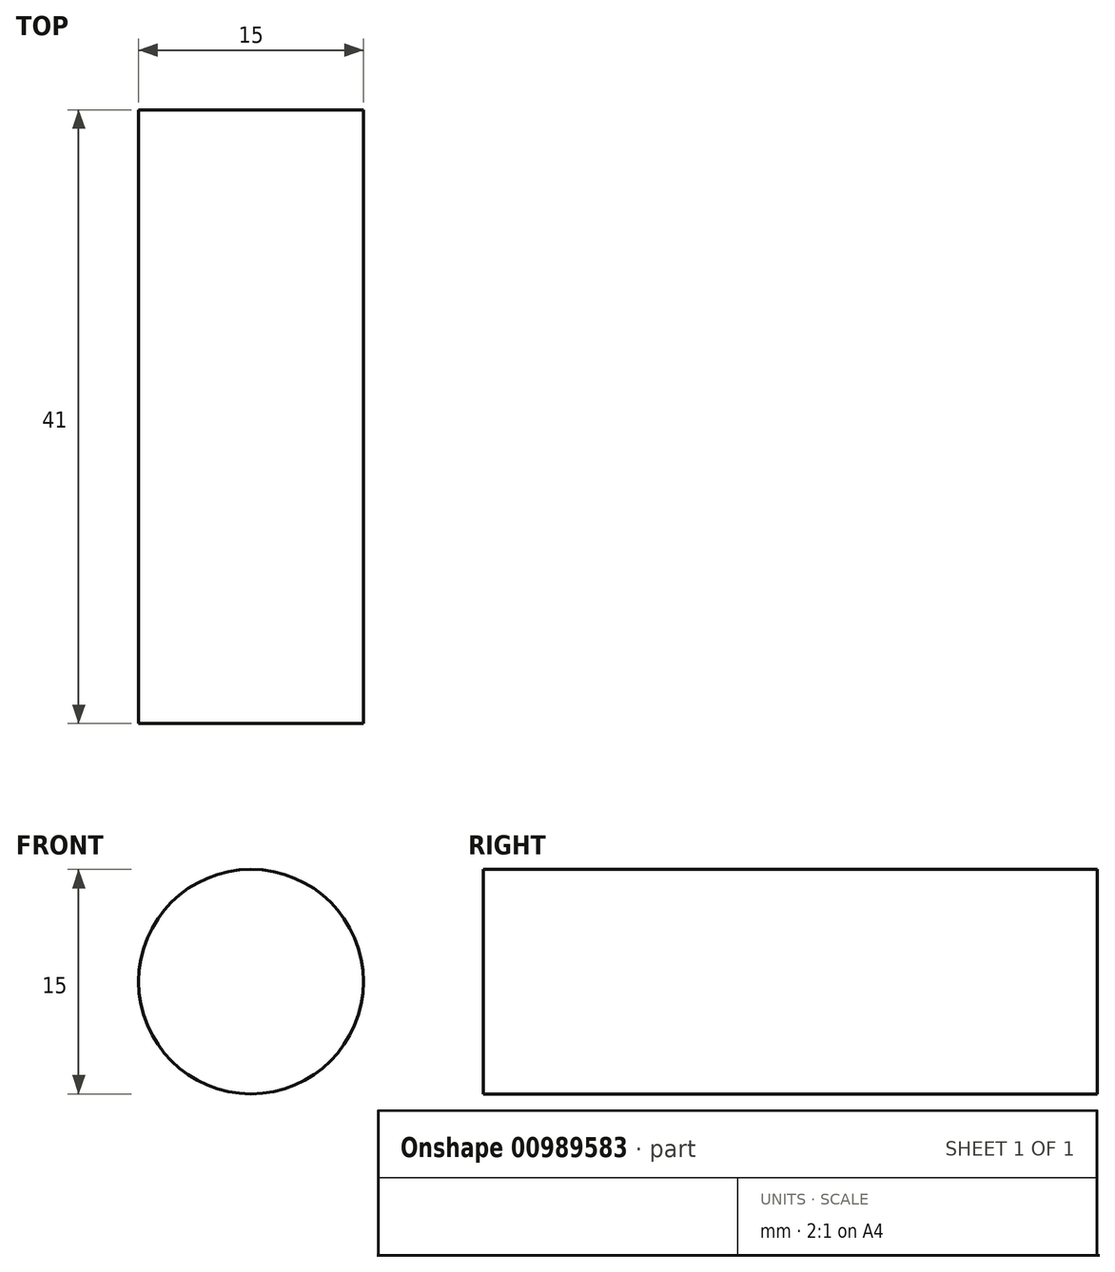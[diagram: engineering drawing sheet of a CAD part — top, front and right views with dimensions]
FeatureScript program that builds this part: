
annotation { "Feature Type Name" : "Feature", "Feature Type Description" : "" }
export const myFeature = defineFeature(function(context is Context, id is Id, definition is map)
    precondition{}
    {
        {
            var Q0;
            Q0=qCreatedBy(makeId("Front.planeOp"),FACE);
            var sketch = newSketch(context, id + "F0", { "sketchPlane" : qUnion([Q0])});
            skCircle(sketch, "E0", {"center": v(0, 0) * mm, "radius": 7.5 * mm});
            skSolve(sketch);
        }
        {
            var Q0;
            Q0 = qSketchRegion(id + "F0", true);
            extrude(context, id + "F1", {"entities" : qUnion([Q0]), "oppositeDirection" : true, "depth" : 41 * mm, "offsetDistance" : 25 * mm});
        }
    });
